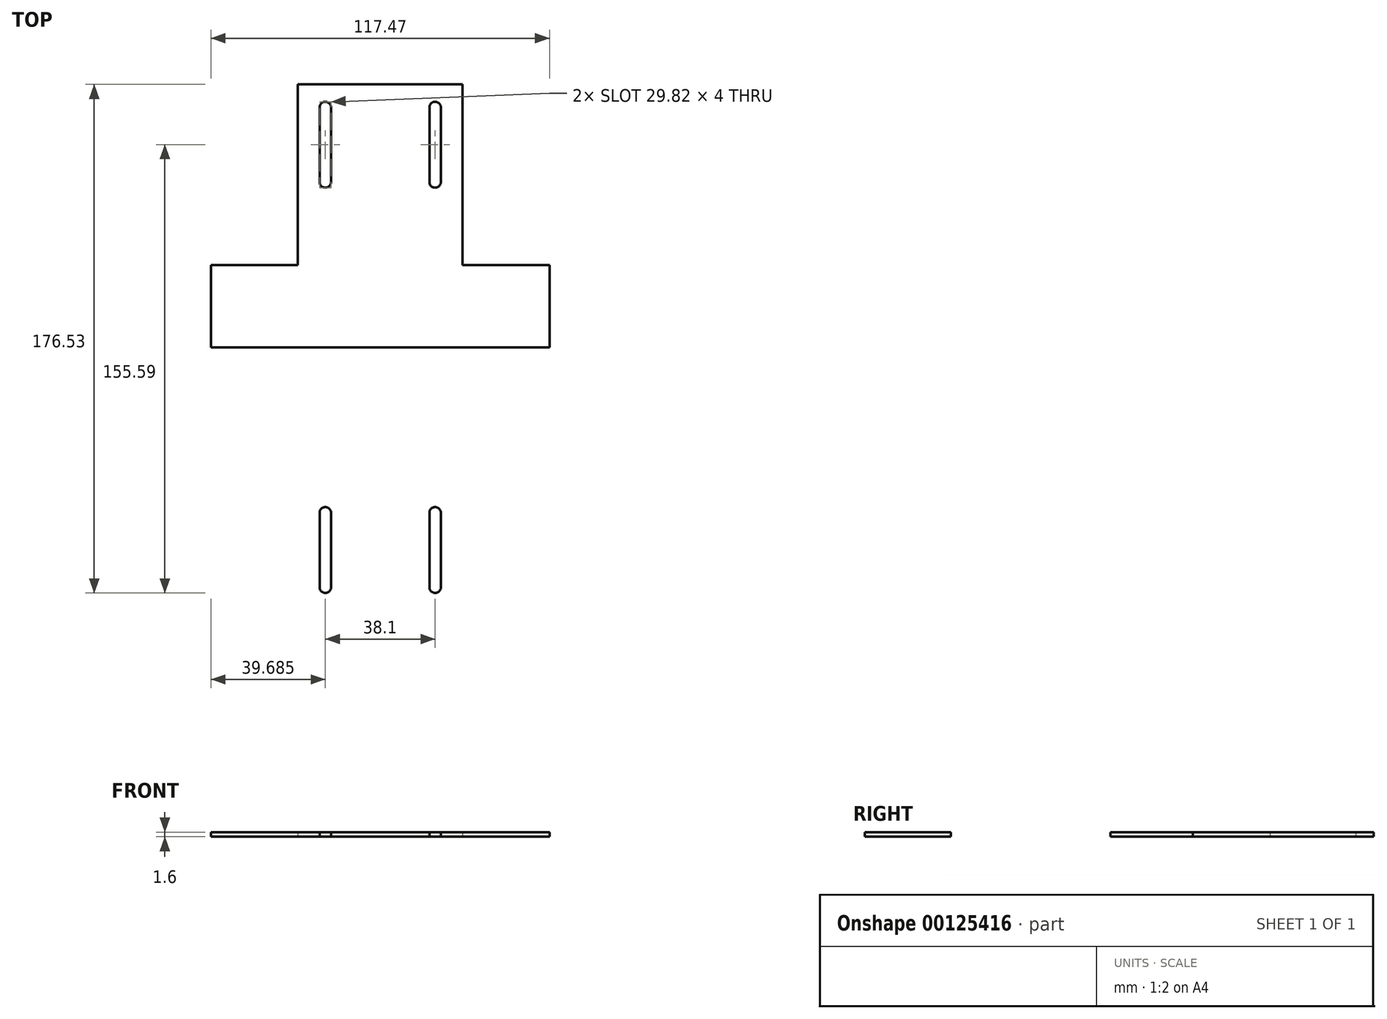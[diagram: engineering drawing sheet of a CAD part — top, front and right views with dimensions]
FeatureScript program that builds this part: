
annotation { "Feature Type Name" : "Feature", "Feature Type Description" : "" }
export const myFeature = defineFeature(function(context is Context, id is Id, definition is map)
    precondition{}
    {
        {
            var Q0;
            Q0=qCreatedBy(makeId("Top.planeOp"),FACE);
            var sketch = newSketch(context, id + "F0", { "sketchPlane" : qUnion([Q0])});
            skLineSegment(sketch, "E0.bottom", {"start": v(0, 0) * mm, "end": v(57.15, 0) * mm});
            skLineSegment(sketch, "E0.top", {"start": v(0, 182.56) * mm, "end": v(57.15, 182.56) * mm});
            skLineSegment(sketch, "E0.left", {"start": v(0, 0) * mm, "end": v(0, 182.56) * mm});
            skLineSegment(sketch, "E0.right", {"start": v(57.15, 0) * mm, "end": v(57.15, 182.56) * mm});
            skLineSegment(sketch, "E1.bottom", {"start": v(87.31, 62.7) * mm, "end": v(-30.16, 62.7) * mm});
            skLineSegment(sketch, "E1.top", {"start": v(87.31, 119.86) * mm, "end": v(-30.16, 119.86) * mm});
            skLineSegment(sketch, "E1.left", {"start": v(87.31, 62.7) * mm, "end": v(87.31, 119.86) * mm});
            skLineSegment(sketch, "E1.right", {"start": v(-30.16, 62.7) * mm, "end": v(-30.16, 119.86) * mm});
            skPoint(sketch, "E1.middle", {"position": v(28.57, 91.28) * mm});
            skPoint(sketch, "E1.middle.positionSnap0", {"position": v(28.57, 182.56) * mm});
            skPoint(sketch, "E1.middle.positionSnap1", {"position": v(0, 91.28) * mm});
            skPoint(sketch, "E1.centerSnap0", {"position": v(28.57, 182.56) * mm});
            skPoint(sketch, "E1.centerSnap1", {"position": v(0, 91.28) * mm});
            skLineSegment(sketch, "E2", {"start": v(57.15, 119.86) * mm, "end": v(57.15, 152.88) * mm});
            skLineSegment(sketch, "E3", {"start": v(57.15, 152.88) * mm, "end": v(87.31, 119.86) * mm});
            skLineSegment(sketch, "E4", {"start": v(57.15, 62.7) * mm, "end": v(57.15, 29.69) * mm});
            skLineSegment(sketch, "E5", {"start": v(57.15, 29.69) * mm, "end": v(87.31, 62.7) * mm});
            skLineSegment(sketch, "E6", {"start": v(0, 62.7) * mm, "end": v(0, 29.69) * mm});
            skLineSegment(sketch, "E7", {"start": v(0, 29.69) * mm, "end": v(-30.16, 62.7) * mm});
            skLineSegment(sketch, "E8", {"start": v(0, 119.86) * mm, "end": v(0, 152.88) * mm});
            skLineSegment(sketch, "E9", {"start": v(0, 152.88) * mm, "end": v(-30.16, 119.86) * mm});
            skSolve(sketch);
        }
        {
            var Q0;
            {var subQ2=sQuery(id+"F0.wireOp",EDGE,"E4");Q0=makeQuery(id+"F0.imprint","IMPRINT",FACE,{"disambiguationData":[TD([[makeQuery(id+"F0.imprint","IMPRINT",EDGE,{"derivedFrom":subQ2}),1.0]])]});}
            var Q1;
            {var subQ2=sQuery(id+"F0.wireOp",EDGE,"E6");Q1=makeQuery(id+"F0.imprint","IMPRINT",FACE,{"disambiguationData":[TD([[makeQuery(id+"F0.imprint","IMPRINT",EDGE,{"derivedFrom":subQ2}),-1.0]])]});}
            var Q2;
            {var subQ2=sQuery(id+"F0.wireOp",EDGE,"E2");Q2=makeQuery(id+"F0.imprint","IMPRINT",FACE,{"disambiguationData":[TD([[makeQuery(id+"F0.imprint","IMPRINT",EDGE,{"derivedFrom":subQ2}),-1.0]])]});}
            var Q3;
            {var subQ2=sQuery(id+"F0.wireOp",EDGE,"E8");Q3=makeQuery(id+"F0.imprint","IMPRINT",FACE,{"disambiguationData":[TD([[makeQuery(id+"F0.imprint","IMPRINT",EDGE,{"derivedFrom":subQ2}),1.0]])]});}
            var Q4;
            {var subQ5=sQuery(id+"F0.wireOp",EDGE,"E0.bottom");Q4=makeQuery(id+"F0.imprint","IMPRINT",FACE,{"disambiguationData":[TD([[makeQuery(id+"F0.imprint","IMPRINT",EDGE,{"derivedFrom":subQ5}),1.0]])]});}
            var Q5;
            {var subQ5=sQuery(id+"F0.wireOp",EDGE,"E1.right");Q5=makeQuery(id+"F0.imprint","IMPRINT",FACE,{"disambiguationData":[TD([[makeQuery(id+"F0.imprint","IMPRINT",EDGE,{"derivedFrom":subQ5}),-1.0]])]});}
            var Q6;
            {var subQ5=sQuery(id+"F0.wireOp",EDGE,"E1.left");Q6=makeQuery(id+"F0.imprint","IMPRINT",FACE,{"disambiguationData":[TD([[makeQuery(id+"F0.imprint","IMPRINT",EDGE,{"derivedFrom":subQ5}),1.0]])]});}
            var Q7;
            {var subQ0=sQuery(id+"F0.wireOp",EDGE,"E1.bottom");var subQ1=sQuery(id+"F0.wireOp",EDGE,"E0.left");var subQ2=makeQuery(id+"F0.imprint","INTERSECT",VERTEX,{"derivedFrom":[subQ1,subQ0,sQuery(id+"F0.wireOp",EDGE,"E6")]});Q7=makeQuery(id+"F0.imprint","IMPRINT",FACE,{"disambiguationData":[TD([[makeQuery(id+"F0.imprint","IMPRINT",EDGE,{"disambiguationData":[TD([[subQ2,-1.0]])],"derivedFrom":subQ1}),-1.0]])]});}
            var Q8;
            {var subQ5=sQuery(id+"F0.wireOp",EDGE,"E0.top");Q8=makeQuery(id+"F0.imprint","IMPRINT",FACE,{"disambiguationData":[TD([[makeQuery(id+"F0.imprint","IMPRINT",EDGE,{"derivedFrom":subQ5}),-1.0]])]});}
            extrude(context, id + "F1", {"entities" : qUnion([Q0, Q1, Q2, Q3, Q4, Q5, Q6, Q7, Q8]), "depth" : 1.6 * mm});
        }
        {
            var Q0;
            Q0=makeQuery(id+"F1.opExtrude","CAP_FACE",FACE,{"disambiguationData":[OSD([sQuery(id+"F0.wireOp",EDGE,"E0.bottom"),sQuery(id+"F0.wireOp",EDGE,"E0.top"),sQuery(id+"F0.wireOp",EDGE,"E0.left"),sQuery(id+"F0.wireOp",EDGE,"E0.right"),sQuery(id+"F0.wireOp",EDGE,"E1.left"),sQuery(id+"F0.wireOp",EDGE,"E1.right"),sQuery(id+"F0.wireOp",EDGE,"E3"),sQuery(id+"F0.wireOp",EDGE,"E5"),sQuery(id+"F0.wireOp",EDGE,"E7"),sQuery(id+"F0.wireOp",EDGE,"E9")])],"isStart":false});
            var sketch = newSketch(context, id + "F2", { "sketchPlane" : qUnion([Q0])});
            skLineSegment(sketch, "E10", {"start": v(57.15, 182.56) * mm, "end": v(47.62, 182.56) * mm});
            skLineSegment(sketch, "E11", {"start": v(47.62, 182.56) * mm, "end": v(47.62, 176.53) * mm});
            skLineSegment(sketch, "E12", {"start": v(47.62, 176.53) * mm, "end": v(49.63, 176.53) * mm});
            skLineSegment(sketch, "E13.bottom", {"start": v(47.62, 176.53) * mm, "end": v(47.62, 176.53) * mm});
            skLineSegment(sketch, "E13.top", {"start": v(47.62, 146.71) * mm, "end": v(47.62, 146.71) * mm});
            skLineSegment(sketch, "E13.left", {"start": v(49.63, 174.53) * mm, "end": v(49.63, 148.71) * mm});
            skLineSegment(sketch, "E13.right", {"start": v(45.62, 174.53) * mm, "end": v(45.62, 148.71) * mm});
            skPoint(sketch, "E14.visualSharp", {"position": v(45.62, 146.71) * mm});
            skArc(sketch, "E14.filletArc", {"start": v(45.62, 148.71) * mm, "mid": v(46.21, 147.3) * mm, "end": v(47.62, 146.71) * mm});
            skPoint(sketch, "E15.visualSharp", {"position": v(49.63, 146.71) * mm});
            skArc(sketch, "E15.filletArc", {"start": v(47.62, 146.71) * mm, "mid": v(49.04, 147.3) * mm, "end": v(49.63, 148.71) * mm});
            skPoint(sketch, "E16.visualSharp", {"position": v(49.63, 176.53) * mm});
            skArc(sketch, "E16.filletArc", {"start": v(49.63, 174.53) * mm, "mid": v(49.04, 175.94) * mm, "end": v(47.62, 176.53) * mm});
            skPoint(sketch, "E17.visualSharp", {"position": v(45.62, 176.53) * mm});
            skArc(sketch, "E17.filletArc", {"start": v(47.62, 176.53) * mm, "mid": v(46.21, 175.94) * mm, "end": v(45.62, 174.53) * mm});
            skLineSegment(sketch, "E18", {"start": v(9.52, 182.56) * mm, "end": v(9.52, 176.53) * mm});
            skLineSegment(sketch, "E19", {"start": v(9.53, 176.53) * mm, "end": v(11.53, 176.53) * mm});
            skLineSegment(sketch, "E20.bottom", {"start": v(9.53, 176.53) * mm, "end": v(9.53, 176.53) * mm});
            skLineSegment(sketch, "E20.top", {"start": v(9.53, 146.71) * mm, "end": v(9.53, 146.71) * mm});
            skLineSegment(sketch, "E20.left", {"start": v(11.53, 174.53) * mm, "end": v(11.53, 148.71) * mm});
            skLineSegment(sketch, "E20.right", {"start": v(7.52, 174.53) * mm, "end": v(7.52, 148.71) * mm});
            skPoint(sketch, "E21.visualSharp", {"position": v(7.52, 146.71) * mm});
            skArc(sketch, "E21.filletArc", {"start": v(7.52, 148.71) * mm, "mid": v(8.11, 147.3) * mm, "end": v(9.53, 146.71) * mm});
            skPoint(sketch, "E22.visualSharp", {"position": v(11.53, 146.71) * mm});
            skArc(sketch, "E22.filletArc", {"start": v(9.53, 146.71) * mm, "mid": v(10.94, 147.3) * mm, "end": v(11.53, 148.71) * mm});
            skPoint(sketch, "E23.visualSharp", {"position": v(11.53, 176.53) * mm});
            skArc(sketch, "E23.filletArc", {"start": v(11.53, 174.53) * mm, "mid": v(10.94, 175.94) * mm, "end": v(9.53, 176.53) * mm});
            skPoint(sketch, "E24.visualSharp", {"position": v(7.52, 176.53) * mm});
            skArc(sketch, "E24.filletArc", {"start": v(9.53, 176.53) * mm, "mid": v(8.11, 175.94) * mm, "end": v(7.52, 174.53) * mm});
            skLineSegment(sketch, "E25.MirrorCS", {"start": v(0, 182.56) * mm, "end": v(9.52, 182.56) * mm});
            skLineSegment(sketch, "E26", {"start": v(-30.16, 91.28) * mm, "end": v(87.31, 91.28) * mm});
            skLineSegment(sketch, "E27.MirrorCS", {"start": v(9.53, 6.03) * mm, "end": v(11.53, 6.03) * mm});
            skArc(sketch, "E28.MirrorCS", {"start": v(47.63, 6.03) * mm, "mid": v(46.21, 6.62) * mm, "end": v(45.62, 8.03) * mm});
            skLineSegment(sketch, "E29.MirrorCS", {"start": v(47.63, 0) * mm, "end": v(47.63, 6.03) * mm});
            skArc(sketch, "E30.MirrorCS", {"start": v(9.53, 6.03) * mm, "mid": v(8.11, 6.62) * mm, "end": v(7.52, 8.03) * mm});
            skArc(sketch, "E31.MirrorCS", {"start": v(11.53, 8.03) * mm, "mid": v(10.94, 6.62) * mm, "end": v(9.53, 6.03) * mm});
            skArc(sketch, "E32.MirrorCS", {"start": v(49.63, 8.03) * mm, "mid": v(49.04, 6.62) * mm, "end": v(47.63, 6.03) * mm});
            skLineSegment(sketch, "E33.MirrorCS", {"start": v(47.63, 6.03) * mm, "end": v(49.63, 6.03) * mm});
            skLineSegment(sketch, "E34.MirrorCS", {"start": v(9.53, 0) * mm, "end": v(9.53, 6.03) * mm});
            skArc(sketch, "E35.MirrorCS", {"start": v(9.53, 35.85) * mm, "mid": v(10.94, 35.27) * mm, "end": v(11.53, 33.85) * mm});
            skArc(sketch, "E36.MirrorCS", {"start": v(45.62, 33.85) * mm, "mid": v(46.21, 35.27) * mm, "end": v(47.63, 35.85) * mm});
            skArc(sketch, "E37.MirrorCS", {"start": v(7.52, 33.85) * mm, "mid": v(8.11, 35.27) * mm, "end": v(9.53, 35.85) * mm});
            skArc(sketch, "E38.MirrorCS", {"start": v(47.62, 35.85) * mm, "mid": v(49.04, 35.27) * mm, "end": v(49.63, 33.85) * mm});
            skLineSegment(sketch, "E39.MirrorCS", {"start": v(9.53, 6.03) * mm, "end": v(9.53, 6.03) * mm});
            skPoint(sketch, "E40.MirrorP", {"position": v(45.62, 6.03) * mm});
            skPoint(sketch, "E41.MirrorP", {"position": v(49.63, 6.03) * mm});
            skPoint(sketch, "E42.MirrorP", {"position": v(11.53, 6.03) * mm});
            skLineSegment(sketch, "E43.MirrorCS", {"start": v(47.63, 6.03) * mm, "end": v(47.63, 6.03) * mm});
            skPoint(sketch, "E44.MirrorP", {"position": v(7.52, 6.03) * mm});
            skPoint(sketch, "E45.MirrorP", {"position": v(49.63, 35.85) * mm});
            skLineSegment(sketch, "E46.MirrorCS", {"start": v(11.53, 8.03) * mm, "end": v(11.53, 33.85) * mm});
            skLineSegment(sketch, "E47.MirrorCS", {"start": v(9.53, 35.85) * mm, "end": v(9.53, 35.85) * mm});
            skLineSegment(sketch, "E48.MirrorCS", {"start": v(7.52, 8.03) * mm, "end": v(7.52, 33.85) * mm});
            skPoint(sketch, "E49.MirrorP", {"position": v(11.53, 35.85) * mm});
            skLineSegment(sketch, "E50.MirrorCS", {"start": v(49.63, 8.03) * mm, "end": v(49.63, 33.85) * mm});
            skLineSegment(sketch, "E51.MirrorCS", {"start": v(45.62, 8.03) * mm, "end": v(45.62, 33.85) * mm});
            skLineSegment(sketch, "E52.MirrorCS", {"start": v(47.62, 35.85) * mm, "end": v(47.63, 35.85) * mm});
            skPoint(sketch, "E53.MirrorP", {"position": v(45.62, 35.85) * mm});
            skPoint(sketch, "E54.MirrorP", {"position": v(7.52, 35.85) * mm});
            skSolve(sketch);
        }
        {
            var Q0;
            Q0=makeQuery(id+"F2.imprint","IMPRINT",FACE,{"disambiguationData":[TD([[makeQuery(id+"F2.imprint","IMPRINT",EDGE,{"derivedFrom":sQuery(id+"F2.wireOp",EDGE,"E20.left")}),-1.0]])]});
            var Q1;
            Q1=makeQuery(id+"F2.imprint","IMPRINT",FACE,{"disambiguationData":[TD([[makeQuery(id+"F2.imprint","IMPRINT",EDGE,{"derivedFrom":sQuery(id+"F2.wireOp",EDGE,"E13.left")}),-1.0]])]});
            var Q2;
            Q2=makeQuery(id+"F2.imprint","IMPRINT",FACE,{"disambiguationData":[TD([[makeQuery(id+"F2.imprint","IMPRINT",EDGE,{"derivedFrom":sQuery(id+"F2.wireOp",EDGE,"E30.MirrorCS")}),-1.0]])]});
            var Q3;
            Q3=makeQuery(id+"F2.imprint","IMPRINT",FACE,{"disambiguationData":[TD([[makeQuery(id+"F2.imprint","IMPRINT",EDGE,{"derivedFrom":sQuery(id+"F2.wireOp",EDGE,"E28.MirrorCS")}),-1.0]])]});
            extrude(context, id + "F3", {"entities" : qUnion([Q0, Q1, Q2, Q3]), "operationType" : NewBodyOperationType.REMOVE, "endBound" : BoundingType.THROUGH_ALL, "oppositeDirection" : true, "depth" : 25.4 * mm});
        }
    });
